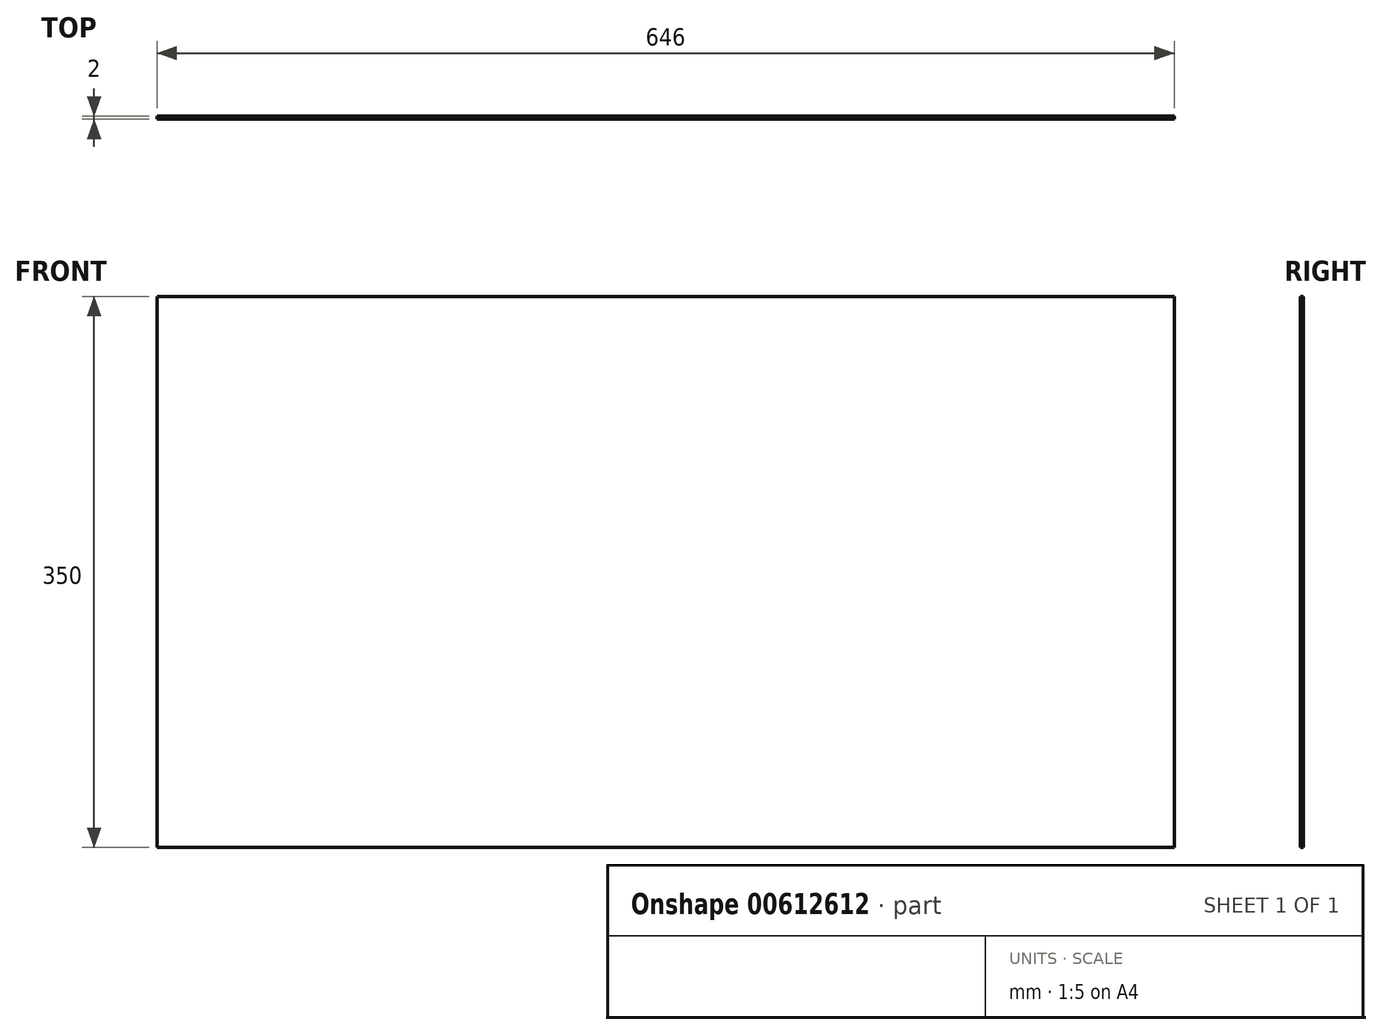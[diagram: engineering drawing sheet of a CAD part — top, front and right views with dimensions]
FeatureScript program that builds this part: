
annotation { "Feature Type Name" : "Feature", "Feature Type Description" : "" }
export const myFeature = defineFeature(function(context is Context, id is Id, definition is map)
    precondition{}
    {
        {
            var Q0;
            Q0=qCreatedBy(makeId("Front.planeOp"),FACE);
            var sketch = newSketch(context, id + "F0", { "sketchPlane" : qUnion([Q0])});
            skLineSegment(sketch, "E0.bottom", {"start": v(-323, 175) * mm, "end": v(323, 175) * mm});
            skLineSegment(sketch, "E0.top", {"start": v(-323, -175) * mm, "end": v(323, -175) * mm});
            skLineSegment(sketch, "E0.left", {"start": v(-323, 175) * mm, "end": v(-323, -175) * mm});
            skLineSegment(sketch, "E0.right", {"start": v(323, 175) * mm, "end": v(323, -175) * mm});
            skPoint(sketch, "E0.middle", {"position": v(0, 0) * mm});
            skLineSegment(sketch, "E1.bottom", {"start": v(-323, 175) * mm, "end": v(-263, 175) * mm});
            skLineSegment(sketch, "E1.top", {"start": v(-323, 325) * mm, "end": v(-263, 325) * mm});
            skLineSegment(sketch, "E1.left", {"start": v(-323, 175) * mm, "end": v(-323, 325) * mm});
            skLineSegment(sketch, "E1.right", {"start": v(-263, 175) * mm, "end": v(-263, 325) * mm});
            skSolve(sketch);
        }
        {
            var Q0;
            Q0=makeQuery(id+"F0.imprint","IMPRINT",FACE,{"disambiguationData":[TD([[makeQuery(id+"F0.imprint","IMPRINT",EDGE,{"derivedFrom":sQuery(id+"F0.wireOp",EDGE,"E0.bottom")}),-1.0]])]});
            var Q1;
            Q1=makeQuery(id+"F0.imprint","IMPRINT",FACE,{"disambiguationData":[TD([[makeQuery(id+"F0.imprint","IMPRINT",EDGE,{"derivedFrom":sQuery(id+"F0.wireOp",EDGE,"E1.bottom")}),1.0]])]});
            extrude(context, id + "F1", {"entities" : qUnion([Q0, Q1]), "depth" : 2 * mm, "offsetDistance" : 25.4 * mm});
        }
    });
